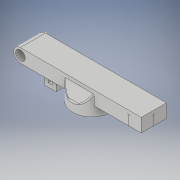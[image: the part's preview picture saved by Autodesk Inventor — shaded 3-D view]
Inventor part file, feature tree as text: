
AUTODESK INVENTOR PART (.ipt)
format: ipt  version: 2019 (Build 230136000, 136)  size: 250,880 bytes
history: native  units: in
note: dims shown in document units (in); Inventor stores cm internally (conversion verified against a paired STEP export)
features: sketch x9, extrude x5, chamfer x2, fillet x2
ambient origin geometry x8: Origin, YZ Plane, XZ Plane, XY Plane, X Axis, Y Axis, Z Axis, Center Point
bodies: Solid1 (feature_tree)
feature tree (18):
  extrude  "Extrusion1"  Depth=2.4606in
  extrude  "Extrusion2"  Depth=0.5118in TaperAngle=0.0deg
  extrude  "Extrusion3"  Depth=0.1969in TaperAngle=0.0deg
  sketch  "Sketch4"  dims[d9=2.2047in]
  chamfer  "Chamfer1"  Distance=0.1969in
  chamfer  "Chamfer2"  Distance=0.1181in Angle=120.0deg
  extrude  "Extrusion4"  Depth=0.0787in TaperAngle=0.0deg
  fillet  "Fillet2"  Radius=0.0394in
  fillet  "Fillet3"  Radius=0.0394in
  sketch  "Sketch6"  dims[d15=0.2559in]
  sketch  "Sketch7"  dims[d16=0.2559in d17=0.1181in d18=0.0787in d19=120.0deg]
  sketch  "Sketch8"  dims[d20=0.1181in d21=0.0787in d22=120.0deg d25=0.315in d26=0.0in d28=0.0394in d29=0.0394in]
  sketch  "Sketch9"  dims[d30=1.3386in d32=0.2362in d33=0.1575in d34=0.315in d35=0.1772in d36=0.0787in d37=0.0787in d39=0.2362in d41=0.1181in d42=0.1575in d43=0.0in]
  extrude  "Extrusion5"  Depth=0.1181in
  sketch  "Sketch1"  dims[d0=0.1969in d2=2.4606in]
  sketch  "Sketch2"  dims[d3=0.1378in d4=0.5118in d5=0.0in]
  sketch  "Sketch3"  dims[d6=0.5118in d7=0.1969in d8=0.0in]
  sketch  "Sketch5"  dims[d11=0.7874in d13=0.1969in d14=0.0in]
